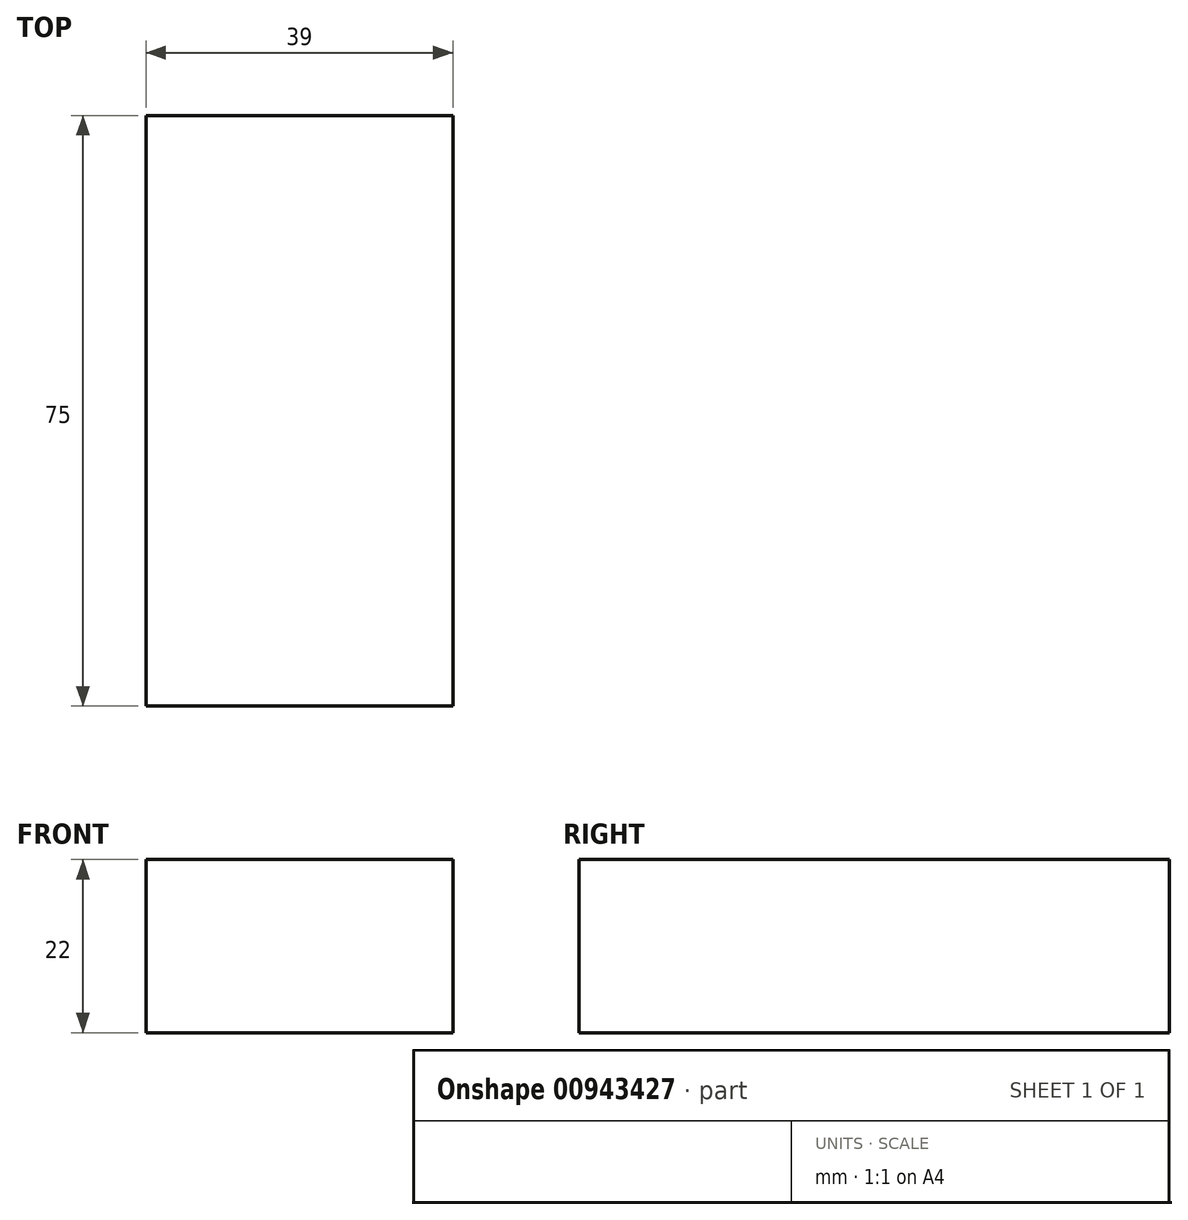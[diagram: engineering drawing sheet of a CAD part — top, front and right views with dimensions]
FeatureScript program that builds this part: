
annotation { "Feature Type Name" : "Feature", "Feature Type Description" : "" }
export const myFeature = defineFeature(function(context is Context, id is Id, definition is map)
    precondition{}
    {
        {
            var Q0;
            Q0=qCreatedBy(makeId("Right.planeOp"),FACE);
            var sketch = newSketch(context, id + "F0", { "sketchPlane" : qUnion([Q0])});
            skLineSegment(sketch, "E0.bottom", {"start": v(0, 0) * mm, "end": v(-75, 0) * mm});
            skLineSegment(sketch, "E0.top", {"start": v(0, 22) * mm, "end": v(-75, 22) * mm});
            skLineSegment(sketch, "E0.left", {"start": v(0, 0) * mm, "end": v(0, 22) * mm});
            skLineSegment(sketch, "E0.right", {"start": v(-75, 0) * mm, "end": v(-75, 22) * mm});
            skSolve(sketch);
        }
        {
            var Q0;
            Q0=makeQuery(id+"F0.imprint","IMPRINT",FACE,{"disambiguationData":[TD([[makeQuery(id+"F0.imprint","IMPRINT",EDGE,{"derivedFrom":sQuery(id+"F0.wireOp",EDGE,"E0.bottom")}),-1.0]])]});
            extrude(context, id + "F1", {"entities" : qUnion([Q0]), "depth" : 39 * mm, "offsetDistance" : 25.4 * mm});
        }
    });
